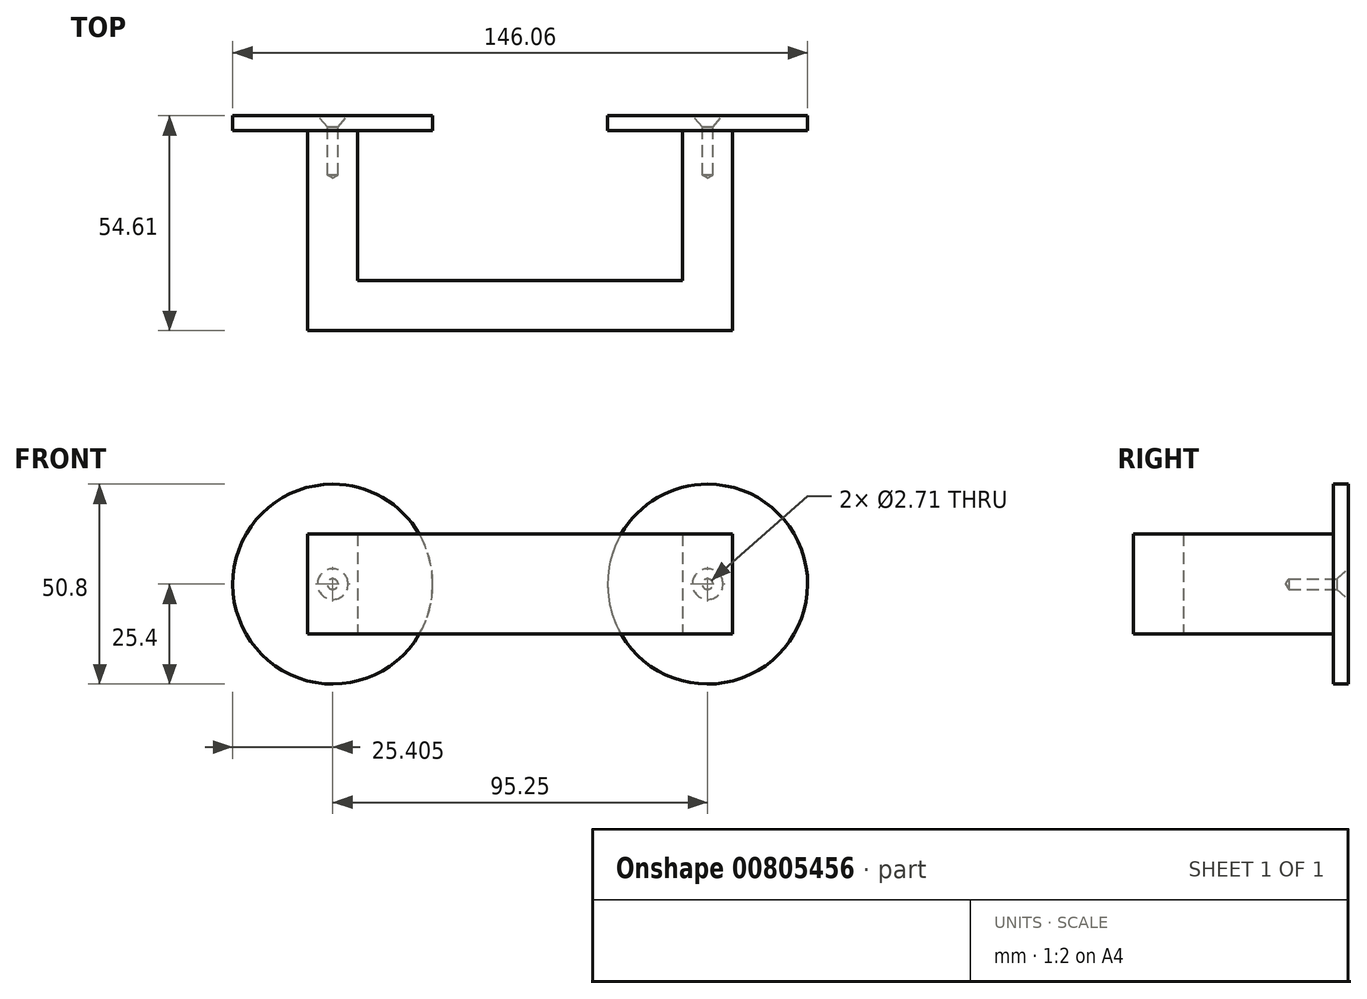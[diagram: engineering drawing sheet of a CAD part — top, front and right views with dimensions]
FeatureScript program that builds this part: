
annotation { "Feature Type Name" : "Feature", "Feature Type Description" : "" }
export const myFeature = defineFeature(function(context is Context, id is Id, definition is map)
    precondition{}
    {
        {
            var Q0;
            Q0=qCreatedBy(makeId("Top.planeOp"),FACE);
            var sketch = newSketch(context, id + "F0", { "sketchPlane" : qUnion([Q0])});
            skLineSegment(sketch, "E0", {"start": v(-41.28, 0) * mm, "end": v(41.28, 0) * mm});
            skPoint(sketch, "E1", {"position": v(0, 0) * mm});
            skLineSegment(sketch, "E2", {"start": v(-41.28, 0) * mm, "end": v(-41.28, 38.1) * mm});
            skLineSegment(sketch, "E3", {"start": v(-41.28, 38.1) * mm, "end": v(-53.98, 38.1) * mm});
            skLineSegment(sketch, "E4", {"start": v(-53.98, 38.1) * mm, "end": v(-53.98, -12.7) * mm});
            skLineSegment(sketch, "E5", {"start": v(41.28, 0) * mm, "end": v(41.27, 38.1) * mm});
            skLineSegment(sketch, "E6", {"start": v(41.27, 38.1) * mm, "end": v(53.98, 38.1) * mm});
            skLineSegment(sketch, "E7", {"start": v(53.98, 38.1) * mm, "end": v(53.98, -12.7) * mm});
            skLineSegment(sketch, "E8", {"start": v(-53.98, -12.7) * mm, "end": v(53.98, -12.7) * mm});
            skSolve(sketch);
        }
        {
            var Q0;
            Q0=makeQuery(id+"F0.imprint","IMPRINT",FACE,{"disambiguationData":[TD([[makeQuery(id+"F0.imprint","IMPRINT",EDGE,{"derivedFrom":sQuery(id+"F0.wireOp",EDGE,"E0")}),-1.0]])]});
            extrude(context, id + "F1", {"entities" : qUnion([Q0]), "endBound" : BoundingType.SYMMETRIC, "depth" : 25.4 * mm, "offsetDistance" : 25.4 * mm});
        }
        {
            var Q0;
            Q0=makeQuery(id+"F1.opExtrude","SWEPT_FACE",FACE,{"disambiguationData":[OSD([sQuery(id+"F0.wireOp",EDGE,"E6")])]});
            var sketch = newSketch(context, id + "F2", { "sketchPlane" : qUnion([Q0])});
            skLineSegment(sketch, "E9", {"start": v(-47.63, 12.7) * mm, "end": v(-47.63, -12.7) * mm, "construction": true});
            skCircle(sketch, "E10", {"center": v(-47.62, 0) * mm, "radius": 25.4 * mm});
            skLineSegment(sketch, "E11", {"start": v(-41.28, -12.7) * mm, "end": v(-53.98, 12.7) * mm, "construction": true});
            skSolve(sketch);
        }
        {
            var Q0;
            Q0=makeQuery(id+"F1.opExtrude","SWEPT_FACE",FACE,{"disambiguationData":[OSD([sQuery(id+"F0.wireOp",EDGE,"E3")])]});
            var sketch = newSketch(context, id + "F3", { "sketchPlane" : qUnion([Q0])});
            skLineSegment(sketch, "E12", {"start": v(47.63, 12.7) * mm, "end": v(47.63, -12.7) * mm, "construction": true});
            skCircle(sketch, "E13", {"center": v(47.63, 0) * mm, "radius": 25.4 * mm});
            skLineSegment(sketch, "E14", {"start": v(41.28, 12.7) * mm, "end": v(53.98, -12.7) * mm, "construction": true});
            skSolve(sketch);
        }
        {
            var Q0;
            {var subQ0=sQuery(id+"F0.wireOp",EDGE,"E3");Q0=makeQuery(id+"F3.imprint","IMPRINT",FACE,{"disambiguationData":[TD([[makeQuery(id+"F3.imprint","IMPRINT",EDGE,{"derivedFrom":makeQuery(id+"F1.opExtrude","CAP_EDGE",EDGE,{"disambiguationData":[OSD([subQ0])],"isStart":true})}),1.0]])]});}
            var Q1;
            Q1=makeQuery(id+"F3.imprint","IMPRINT",FACE,{"disambiguationData":[TD([[makeQuery(id+"F3.imprint","IMPRINT",EDGE,{"derivedFrom":sQuery(id+"F3.wireOp",EDGE,"E13")}),1.0]])]});
            var Q2;
            {var subQ0=sQuery(id+"F0.wireOp",EDGE,"E6");Q2=makeQuery(id+"F2.imprint","IMPRINT",FACE,{"disambiguationData":[TD([[makeQuery(id+"F2.imprint","IMPRINT",EDGE,{"derivedFrom":makeQuery(id+"F1.opExtrude","CAP_EDGE",EDGE,{"disambiguationData":[OSD([subQ0])],"isStart":true})}),-1.0]])]});}
            var Q3;
            Q3=makeQuery(id+"F2.imprint","IMPRINT",FACE,{"disambiguationData":[TD([[makeQuery(id+"F2.imprint","IMPRINT",EDGE,{"derivedFrom":sQuery(id+"F2.wireOp",EDGE,"E10")}),1.0]])]});
            extrude(context, id + "F4", {"entities" : qUnion([Q0, Q1, Q2, Q3]), "operationType" : NewBodyOperationType.ADD, "depth" : 3.8 * mm, "offsetDistance" : 25.4 * mm});
        }
        {
            var Q0;
            Q0=makeQuery(id+"F4.opExtrude","CAP_FACE",FACE,{"disambiguationData":[OSD([sQuery(id+"F2.wireOp",EDGE,"E10")])],"isStart":false});
            var sketch = newSketch(context, id + "F5", { "sketchPlane" : qUnion([Q0])});
            skLineSegment(sketch, "E15", {"start": v(-41.28, -12.7) * mm, "end": v(-53.98, 12.7) * mm, "construction": true});
            skPoint(sketch, "E16", {"position": v(-47.63, 0) * mm});
            skSolve(sketch);
        }
        {
            var Q0;
            Q0=sQuery(id+"F5.wireOp",VERTEX,"E16");
            var Q1;
            Q1=makeQuery(id+"F1.opExtrude","SWEPT_BODY",BODY,{"disambiguationData":[OSD([sQuery(id+"F0.wireOp",EDGE,"E0"),sQuery(id+"F0.wireOp",EDGE,"E2"),sQuery(id+"F0.wireOp",EDGE,"E3"),sQuery(id+"F0.wireOp",EDGE,"E4"),sQuery(id+"F0.wireOp",EDGE,"E5"),sQuery(id+"F0.wireOp",EDGE,"E6"),sQuery(id+"F0.wireOp",EDGE,"E7"),sQuery(id+"F0.wireOp",EDGE,"E8")])]});
            hole(context, id + "F6", {"style" : HoleStyle.C_SINK, "endStyle" : HoleEndStyle.BLIND, "standardTappedOrClearance" : lookupTablePath({ "standard" : "ANSI", "engagement" : "75%", "pitch" : "32 tpi", "size" : "#6", "type" : "Tapped" }), "standardBlindInLast" : lookupTablePath({ "standard" : "ANSI", "engagement" : "75%", "pitch" : "32 tpi", "size" : "#6", "type" : "Tapped" }), "holeDiameter" : 2.7 * mm, "cSinkDiameter" : 7.8 * mm, "cSinkAngle" : 82 * degree, "majorDiameter" : 3.5 * mm, "showTappedDepth" : true, "holeDepth" : 15.08 * mm, "isTappedThrough" : true, "tappedDepth" : 12.7 * mm, "tapClearance" : 3, "locations" : qUnion([Q0]), "scope" : qUnion([Q1])});
        }
        {
            var Q0;
            Q0=makeQuery(id+"F4.opExtrude","CAP_FACE",FACE,{"disambiguationData":[OSD([sQuery(id+"F3.wireOp",EDGE,"E13")])],"isStart":false});
            var sketch = newSketch(context, id + "F7", { "sketchPlane" : qUnion([Q0])});
            skLineSegment(sketch, "E17", {"start": v(41.27, 12.7) * mm, "end": v(53.98, -12.7) * mm, "construction": true});
            skPoint(sketch, "E18", {"position": v(47.63, 0) * mm});
            skSolve(sketch);
        }
        {
            var Q0;
            Q0=sQuery(id+"F7.wireOp",VERTEX,"E18");
            var Q1;
            Q1=makeQuery(id+"F1.opExtrude","SWEPT_BODY",BODY,{"disambiguationData":[OSD([sQuery(id+"F0.wireOp",EDGE,"E0"),sQuery(id+"F0.wireOp",EDGE,"E2"),sQuery(id+"F0.wireOp",EDGE,"E3"),sQuery(id+"F0.wireOp",EDGE,"E4"),sQuery(id+"F0.wireOp",EDGE,"E5"),sQuery(id+"F0.wireOp",EDGE,"E6"),sQuery(id+"F0.wireOp",EDGE,"E7"),sQuery(id+"F0.wireOp",EDGE,"E8")])]});
            hole(context, id + "F8", {"style" : HoleStyle.C_SINK, "endStyle" : HoleEndStyle.BLIND, "standardTappedOrClearance" : lookupTablePath({ "standard" : "ANSI", "engagement" : "75%", "pitch" : "32 tpi", "size" : "#6", "type" : "Tapped" }), "standardBlindInLast" : lookupTablePath({ "standard" : "ANSI", "engagement" : "75%", "pitch" : "32 tpi", "size" : "#6", "type" : "Tapped" }), "holeDiameter" : 2.7 * mm, "cSinkDiameter" : 7.8 * mm, "cSinkAngle" : 82 * degree, "majorDiameter" : 3.5 * mm, "showTappedDepth" : true, "holeDepth" : 15.1 * mm, "isTappedThrough" : true, "tappedDepth" : 12.7 * mm, "tapClearance" : 3, "locations" : qUnion([Q0]), "scope" : qUnion([Q1])});
        }
    });
